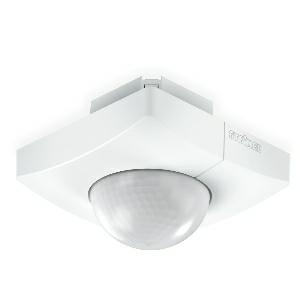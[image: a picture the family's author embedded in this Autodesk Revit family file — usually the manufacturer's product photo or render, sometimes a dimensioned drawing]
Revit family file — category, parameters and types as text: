
# Revit family: is_345_033866
name_source: partatom
category: Elektroinstallationen
revit_build: Autodesk Revit 2016 (Build: 20190508_0715(x64)
units: mm (PartAtom-declared; Revit-internal decimal feet)

## family parameters
Basisbauteil = Fläche
Beim Laden mit Abzugskörper schneiden = Nein
Bemaßung runder Anschluss = Durchmesser verwenden
Beschriftungsausrichtung beibehalten = Nein
Gemeinsam genutzt = Nein
Raumberechnungspunkt = Nein
Teiletyp = Normal

## types (1)
- IS 345
    Apparent Load = 0 VA
    Beschreibung = Type: Motion detectors; Dimensions (L x W x H): 78 x 94 x 94 mm; Mains power supply: 220 – 240 V / 50 – 60 Hz; Sensor Technology: passive infrared; Application, place: Indoors; Application, room: corridor / aisle, multi-storey / underground car park, Indoors; Installation site: ceiling; Installation: Concealed wiring; Switching zones: 280 switching zones; Electronic scalability: No; Mechanical scalability: No; Mounting height: 2,50 – 5,00 m; Optimum mounting height: 2,8 m; Detection angle: 360 °; Angle of aperture: 45 °; Sneak-by guard: Yes; Capability of masking out individual segments: Yes; Reach, radial: 12 x 6 m (72 m²); Reach, tangential: 23 x 6 m (138 m²); Twilight setting TEACH: Yes; Twilight setting: 2 – 1000 lx; Time setting: 5 sec – 15 min; Control output, Dali: Broadcast 1x30 electronic ballasts; Constant-lighting control: Yes; Basic light level function: Yes; Basic light level function in per cent: 10 – 50 %; Basic light level function time: 1-30 min, all night; Basic light level function percentage, from: 10 %; Basic light level function percentage, up to: 50 %; Functions: Normal / test mode, Manual ON / ON-OFF, Constant-lighting control ON-OFF; Settings via: Remote control, Potentiometers, Smart Remote; With remote control: No; Interconnection: Yes; IP-rating: IP20; Material: Plastic; Ambient temperature: -20 – 50 °C; Colour: white; Colour, RAL: 9003; Manufacturer's Warranty: 5 years; Version: DALI-2 Application Controller - concealed, sq.; PU1, EAN: 4007841033866
    Height = 0 mm  [stored 0 ft]
    Hersteller = Steinel
    Length = 78 mm  [stored 0.255906 ft]
    Maximum range = 11.589 m
    ModVariant = Nein
    Modell = 033866
    Mounting Place = Ceiling
    Mounting Type = Recessed
    Number of Poles = 1
    OnlyDefault = Ja
    Power Factor = 1
    Product Name = IS 345
    Product group = Presence detector
    ProductGroupID = 4
    Protection Class = Protection class
    Protection Degree = IP 20
    RlxData = <blob elided: 137661 chars, md5=c41fae0e>
    Sensor characteristics = Stretched
    Sensor type = Passive (infrared)
    SensorDataFile = <blob elided: 5885 chars, md5=98bccc25>
    Type of entry = Motion
    Typenbild = produkt1_033866.jpg
    Typenkommentare = Product without accessories
    URL = http://relux.com
    VarID = ---
    Voltage = 0 V
    Vorgabe-Ansicht = 1800 mm
    Weight = 0.00 kg
    Width = 94 mm  [stored 0.308399 ft]

note: [stored X ft] marks values corroborated as IEEE doubles in the binary element streams (Revit-internal decimal feet)

## geometry (parser evidence)
native form markers: Sweep x17
no freeform markers — native parametric forms only
